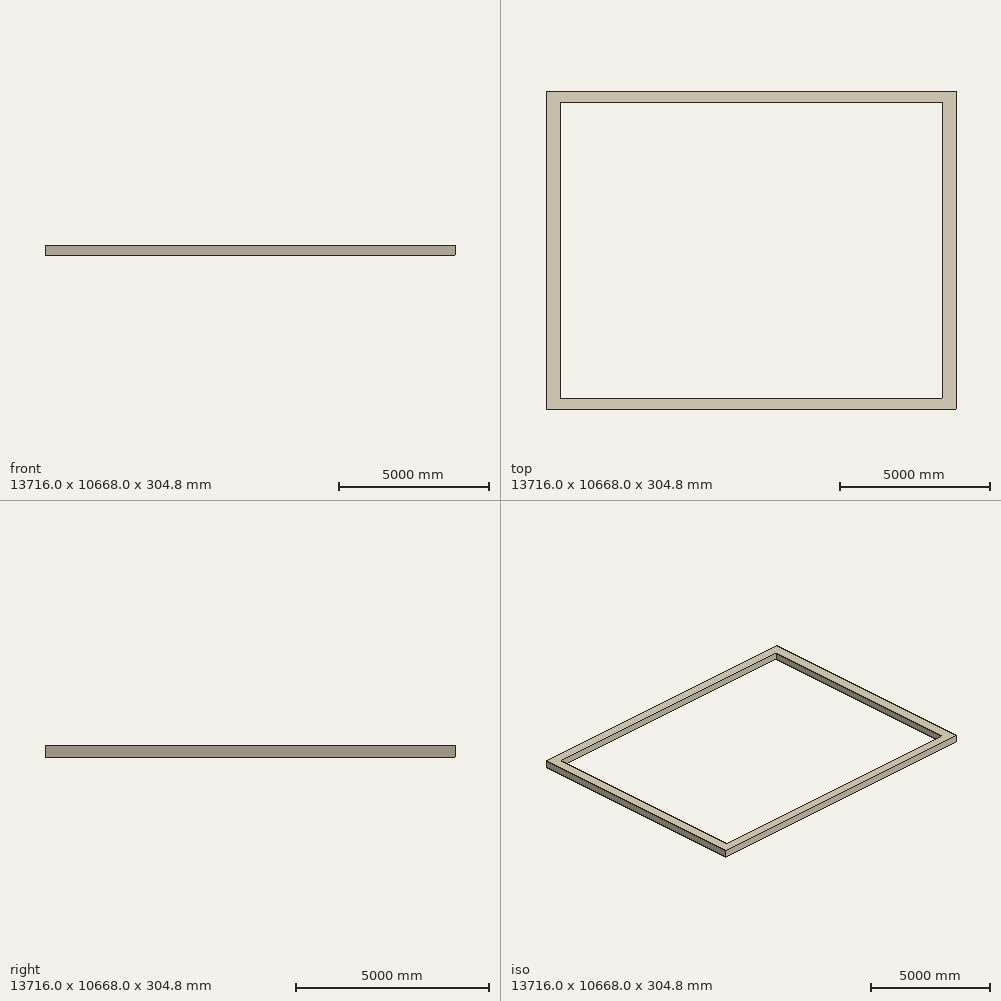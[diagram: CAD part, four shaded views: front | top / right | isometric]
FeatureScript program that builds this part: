
annotation { "Feature Type Name" : "Feature", "Feature Type Description" : "" }
export const myFeature = defineFeature(function(context is Context, id is Id, definition is map)
    precondition{}
    {
        {
            var Q0;
            Q0=qCreatedBy(makeId("Top.planeOp"),FACE);
            var sketch = newSketch(context, id + "F0", { "sketchPlane" : qUnion([Q0])});
            skLineSegment(sketch, "E0.bottom", {"start": v(-6858, 5334) * mm, "end": v(6858, 5334) * mm});
            skLineSegment(sketch, "E0.top", {"start": v(-6858, -5334) * mm, "end": v(6858, -5334) * mm});
            skLineSegment(sketch, "E0.left", {"start": v(-6858, 5334) * mm, "end": v(-6858, -5334) * mm});
            skLineSegment(sketch, "E0.right", {"start": v(6858, 5334) * mm, "end": v(6858, -5334) * mm});
            skPoint(sketch, "E0.middle", {"position": v(0, 0) * mm});
            skLineSegment(sketch, "E1.bottom", {"start": v(-6399.58, 4940.25) * mm, "end": v(6399.58, 4940.25) * mm});
            skLineSegment(sketch, "E1.top", {"start": v(-6399.58, -4940.25) * mm, "end": v(6399.58, -4940.25) * mm});
            skLineSegment(sketch, "E1.left", {"start": v(-6399.58, 4940.25) * mm, "end": v(-6399.58, -4940.25) * mm});
            skLineSegment(sketch, "E1.right", {"start": v(6399.58, 4940.25) * mm, "end": v(6399.58, -4940.25) * mm});
            skSolve(sketch);
        }
        {
            var Q0;
            Q0=makeQuery(id+"F0.imprint","IMPRINT",FACE,{"disambiguationData":[TD([[makeQuery(id+"F0.imprint","IMPRINT",EDGE,{"derivedFrom":sQuery(id+"F0.wireOp",EDGE,"E0.bottom")}),-1.0]])]});
            extrude(context, id + "F1", {"entities" : qUnion([Q0]), "depth" : 304.8 * mm, "offsetDistance" : 25.4 * mm});
        }
    });
